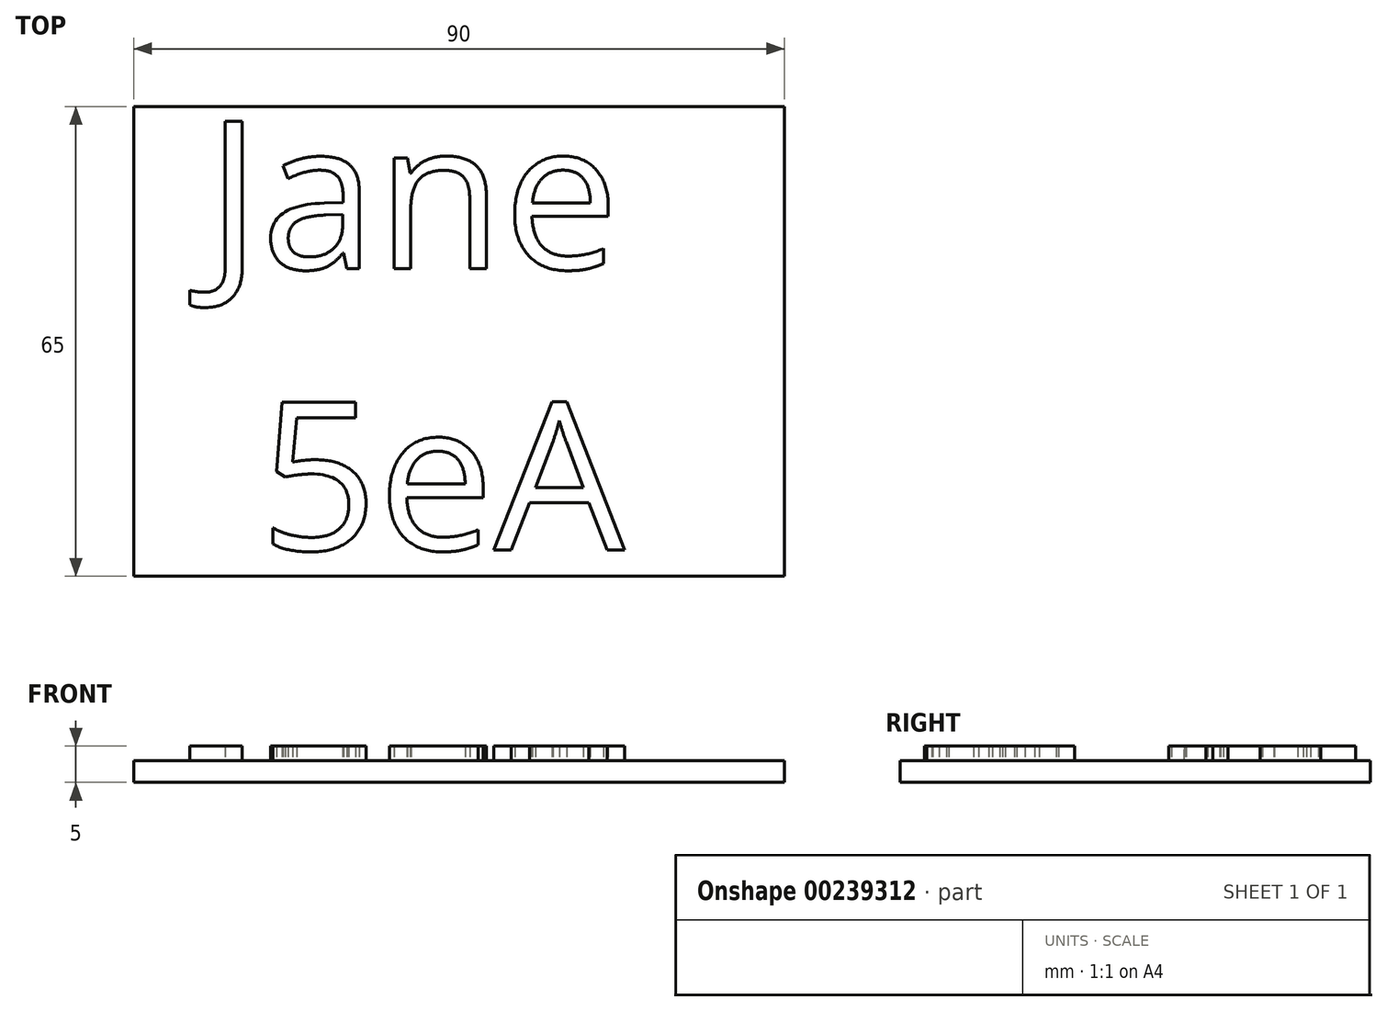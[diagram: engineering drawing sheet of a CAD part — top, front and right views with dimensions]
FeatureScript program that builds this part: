
annotation { "Feature Type Name" : "Feature", "Feature Type Description" : "" }
export const myFeature = defineFeature(function(context is Context, id is Id, definition is map)
    precondition{}
    {
        {
            var Q0;
            Q0=qCreatedBy(makeId("Top.planeOp"),FACE);
            var sketch = newSketch(context, id + "F0", { "sketchPlane" : qUnion([Q0])});
            skLineSegment(sketch, "E0.bottom", {"start": v(0, 0) * mm, "end": v(90, 0) * mm});
            skLineSegment(sketch, "E0.top", {"start": v(0, -65) * mm, "end": v(90, -65) * mm});
            skLineSegment(sketch, "E0.left", {"start": v(0, 0) * mm, "end": v(0, -65) * mm});
            skLineSegment(sketch, "E0.right", {"start": v(90, 0) * mm, "end": v(90, -65) * mm});
            skSolve(sketch);
        }
        {
            var Q0;
            Q0=makeQuery(id+"F0.imprint","IMPRINT",FACE,{"disambiguationData":[TD([[makeQuery(id+"F0.imprint","IMPRINT",EDGE,{"derivedFrom":sQuery(id+"F0.wireOp",EDGE,"E0.bottom")}),-1.0]])]});
            extrude(context, id + "F1", {"entities" : qUnion([Q0]), "depth" : 3 * mm});
        }
        {
            var Q0;
            Q0=makeQuery(id+"F1.opExtrude","CAP_FACE",FACE,{"disambiguationData":[OSD([sQuery(id+"F0.wireOp",EDGE,"E0.bottom"),sQuery(id+"F0.wireOp",EDGE,"E0.top"),sQuery(id+"F0.wireOp",EDGE,"E0.left"),sQuery(id+"F0.wireOp",EDGE,"E0.right")])],"isStart":false});
            var sketch = newSketch(context, id + "F2", { "sketchPlane" : qUnion([Q0])});
            skText(sketch, "E1", { "text": "Jane\n 5eA", "fontName": "OpenSans-Regular.ttf"});
            const initialGuessF2  = {"E1": [0.01, -0.02245, 1, 0, 0.02059]};
            skSetInitialGuess(sketch, initialGuessF2);
            skSolve(sketch);
        }
        {
            var Q0;
            Q0 = qSketchRegion(id + "F2", true);
            extrude(context, id + "F3", {"entities" : qUnion([Q0]), "operationType" : NewBodyOperationType.ADD, "depth" : 2 * mm});
        }
    });
